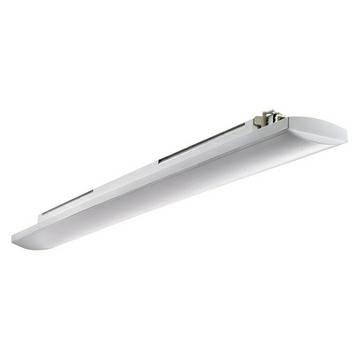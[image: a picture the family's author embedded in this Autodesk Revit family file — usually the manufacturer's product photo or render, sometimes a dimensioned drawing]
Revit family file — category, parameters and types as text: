
# Revit family: Lighting-Industrial-GEWISS-SMART[3]PLUS-HLO-WATERTIGHT-LED-EMERGENCY_OPAL_1600mm
name_source: partatom
category: Apparecchi per illuminazione
units: mm (PartAtom-declared; Revit-internal decimal feet)

## family parameters
Condiviso = No
Host = Superficie
Numero OmniClass = 23.80.70.11
Punto di calcolo locali = No
Quota connettore circolare = Usa diametro
Sorgente d'illuminazione = No
Taglio con vuoti quando caricato = No
Tipo di parte = Normale
Titolo OmniClass = Luminaries for Internal Lighting

## types (1)
- Lighting-Industrial-GEWISS-SMART[3]PLUS-HLO-WATERTIGHT-LED-EMERGENCY_OPAL_1600mm
    Application = Indoor
    Carico apparente = 27 VA
    Catalogue = LIGHTING
    Catalogue Range = SMART[3] PLUS HLO
    Colour temperature = 5700 K (CRI > 90)
    Colour temperature: = 5700 K (CRI > 90)
    Commenti sul wattaggio = 27W
    Descrizione = SMART3 PLUS 1600 EMERG DT1+DT6 HO OPAL 9 57
    Efficiency class of integrated LEDs = A ÷ A++
    Electrocod = 2434
    Ganci = GEWISS  - ALLUMINIO
    Glow Wire Test = 850°C
    IDF = d25070b9-b82a-4119-b79e-2c293114ceb5
    IDT = 42ad88ef-a339-4291-a014-784caecbcb9b
    IP degree = IP66/IP69
    Immagine tipo = GWS3158P.jpg
    Insulation class = II
    Lamp = LED
    Lampada = LED
    Length = 1600 mm
    Lumen output (lm) = 6600
    Lunghezza Lampada = 1600 mm  [stored 5.24934 ft]
    Modello = GWS3325BP957
    Operating temperature: = ND
    Produttore = GEWISS S.p.A.
    Prospetto di default = 1219 mm
    SEO = Ceiling
    Schermo. = Gewiss - Led Acceso
    Shield type = Opal
    Shock resistance = IK08
    Stampa 1_100 = Sì
    Stampa 1_200 = No
    Struttura = GEWISS - SMART 3 - GRIGIO
    System power = 50 W
    Technical sheet = https://www.gewiss.com
    Type of light source = LED - Not replaceable
    URL = https://www.gewiss.com
    Version file RFA = 20.0
    Voltage = 220-240 V
    Warranty = ND
    Working temperature = ND

note: [stored X ft] marks values corroborated as IEEE doubles in the binary element streams (Revit-internal decimal feet)
